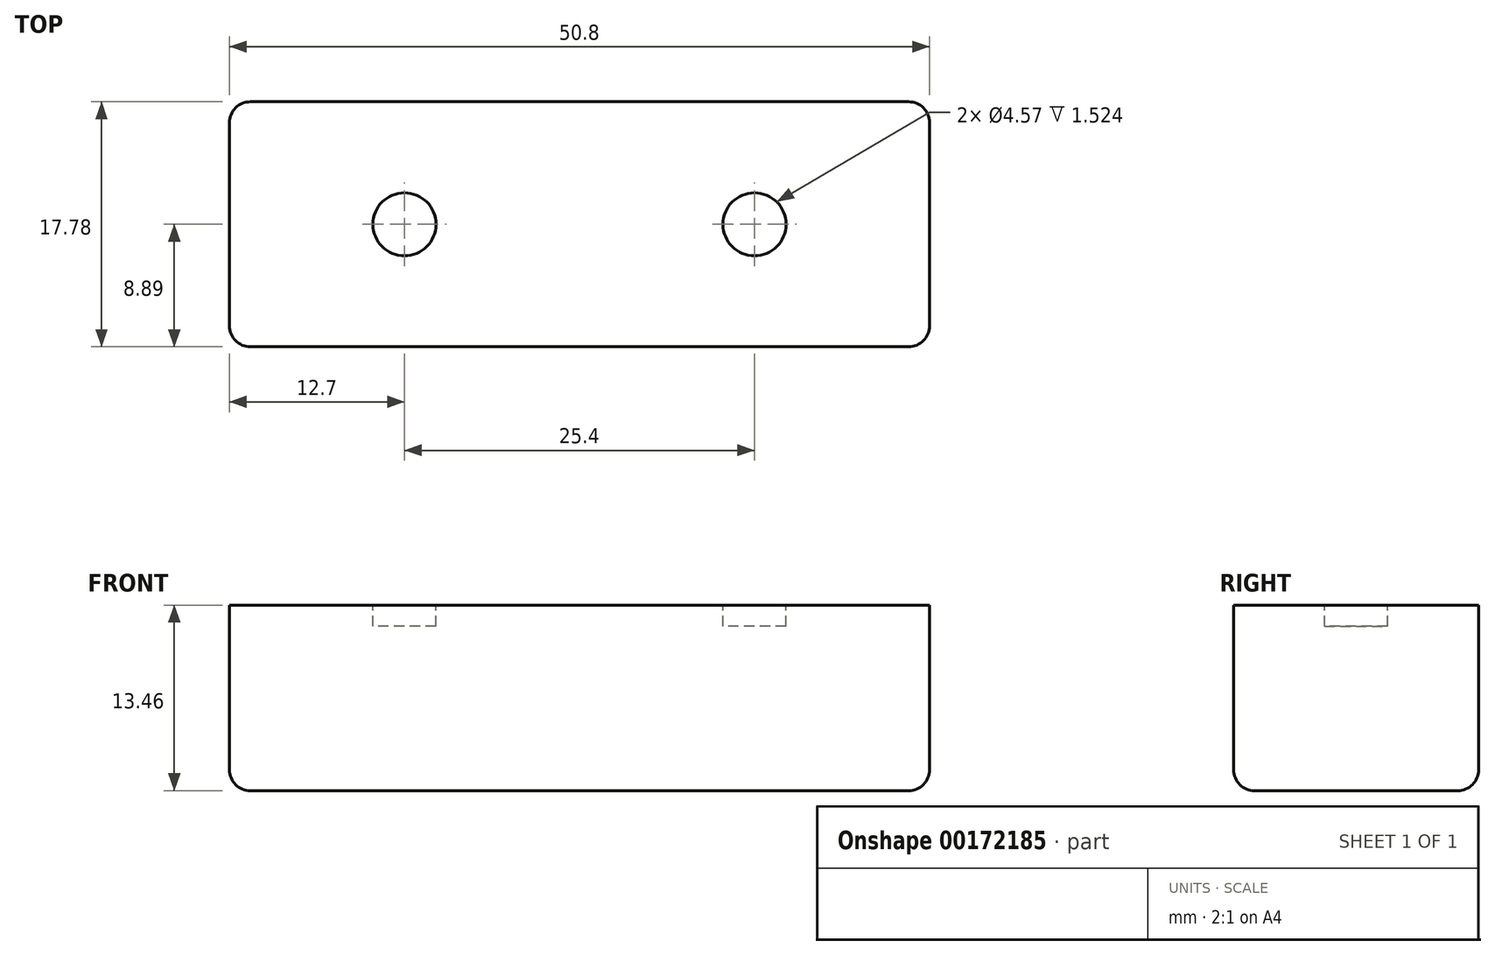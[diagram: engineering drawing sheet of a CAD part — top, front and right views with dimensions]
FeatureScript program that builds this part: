
annotation { "Feature Type Name" : "Feature", "Feature Type Description" : "" }
export const myFeature = defineFeature(function(context is Context, id is Id, definition is map)
    precondition{}
    {
        {
            var Q0;
            Q0=qCreatedBy(makeId("Top.planeOp"),FACE);
            var sketch = newSketch(context, id + "F0", { "sketchPlane" : qUnion([Q0])});
            skLineSegment(sketch, "E0.bottom", {"start": v(-25.4, 8.9) * mm, "end": v(25.4, 8.9) * mm});
            skLineSegment(sketch, "E0.top", {"start": v(-25.4, -8.89) * mm, "end": v(25.4, -8.89) * mm});
            skLineSegment(sketch, "E0.left", {"start": v(-25.4, 8.9) * mm, "end": v(-25.4, -8.9) * mm});
            skLineSegment(sketch, "E0.right", {"start": v(25.4, 8.9) * mm, "end": v(25.4, -8.9) * mm});
            skCircle(sketch, "E1", {"center": v(-12.7, 0) * mm, "radius": 2.29 * mm, "construction": true});
            skCircle(sketch, "E2", {"center": v(12.7, 0) * mm, "radius": 2.29 * mm, "construction": true});
            skLineSegment(sketch, "E3", {"start": v(12.7, 0) * mm, "end": v(-12.7, 0) * mm, "construction": true});
            skPoint(sketch, "E4", {"position": v(0, 0) * mm});
            skPoint(sketch, "E5", {"position": v(0, 8.9) * mm});
            skPoint(sketch, "E6", {"position": v(25.4, 0) * mm});
            skSolve(sketch);
        }
        {
            var Q0;
            Q0 = qSketchRegion(id + "F0", true);
            extrude(context, id + "F1", {"entities" : qUnion([Q0]), "depth" : 13.46 * mm});
        }
        {
            var Q0;
            Q0=makeQuery(id+"F1.opExtrude","CAP_FACE",FACE,{"disambiguationData":[OSD([sQuery(id+"F0.wireOp",EDGE,"E0.bottom"),sQuery(id+"F0.wireOp",EDGE,"E0.top"),sQuery(id+"F0.wireOp",EDGE,"E0.left"),sQuery(id+"F0.wireOp",EDGE,"E0.right")])],"isStart":true});
            var Q1;
            Q1=makeQuery(id+"F1.opExtrude","SWEPT_EDGE",EDGE,{"disambiguationData":[OSD([sQuery(id+"F0.wireOp",EDGE,"E0.top"),sQuery(id+"F0.wireOp",EDGE,"E0.left")])]});
            var Q2;
            Q2=makeQuery(id+"F1.opExtrude","SWEPT_EDGE",EDGE,{"disambiguationData":[OSD([sQuery(id+"F0.wireOp",EDGE,"E0.top"),sQuery(id+"F0.wireOp",EDGE,"E0.right")])]});
            var Q3;
            Q3=makeQuery(id+"F1.opExtrude","SWEPT_EDGE",EDGE,{"disambiguationData":[OSD([sQuery(id+"F0.wireOp",EDGE,"E0.bottom"),sQuery(id+"F0.wireOp",EDGE,"E0.right")])]});
            var Q4;
            Q4=makeQuery(id+"F1.opExtrude","SWEPT_EDGE",EDGE,{"disambiguationData":[OSD([sQuery(id+"F0.wireOp",EDGE,"E0.bottom"),sQuery(id+"F0.wireOp",EDGE,"E0.left")])]});
            fillet(context, id + "F2", {"entities" : qUnion([Q0, Q1, Q2, Q3, Q4]), "radius" : 1.52 * mm, "tangentPropagation" : true, "allowEdgeOverflow" : false});
        }
        {
            var Q0;
            Q0=makeQuery(id+"F1.opExtrude","CAP_FACE",FACE,{"disambiguationData":[OSD([sQuery(id+"F0.wireOp",EDGE,"E0.bottom"),sQuery(id+"F0.wireOp",EDGE,"E0.top"),sQuery(id+"F0.wireOp",EDGE,"E0.left"),sQuery(id+"F0.wireOp",EDGE,"E0.right")])],"isStart":false});
            var sketch = newSketch(context, id + "F3", { "sketchPlane" : qUnion([Q0])});
            skCircle(sketch, "E7", {"center": v(12.7, 0) * mm, "radius": 2.29 * mm});
            skCircle(sketch, "E8", {"center": v(-12.7, 0) * mm, "radius": 2.29 * mm});
            skSolve(sketch);
        }
        {
            var Q0;
            Q0 = qSketchRegion(id + "F3", true);
            extrude(context, id + "F4", {"entities" : qUnion([Q0]), "operationType" : NewBodyOperationType.REMOVE, "oppositeDirection" : true, "depth" : 1.52 * mm});
        }
    });
